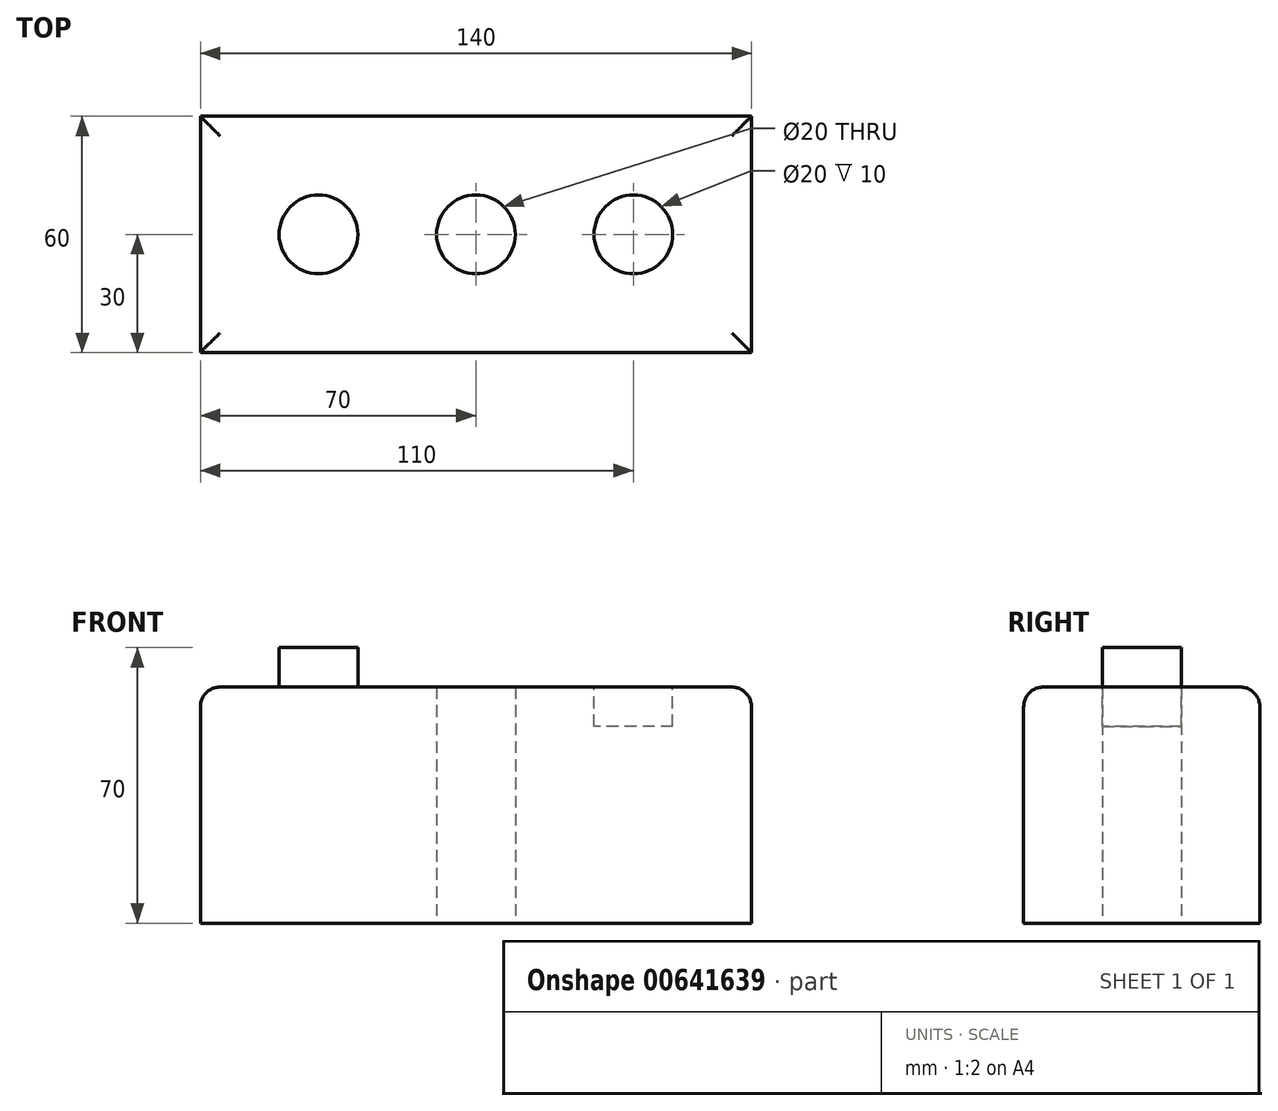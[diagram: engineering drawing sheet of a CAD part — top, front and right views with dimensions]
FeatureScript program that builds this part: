
annotation { "Feature Type Name" : "Feature", "Feature Type Description" : "" }
export const myFeature = defineFeature(function(context is Context, id is Id, definition is map)
    precondition{}
    {
        {
            var Q0;
            Q0=qCreatedBy(makeId("Top.planeOp"),FACE);
            var sketch = newSketch(context, id + "F0", { "sketchPlane" : qUnion([Q0])});
            skLineSegment(sketch, "E0.bottom", {"start": v(70, -30) * mm, "end": v(-70, -30) * mm});
            skLineSegment(sketch, "E0.top", {"start": v(70, 30) * mm, "end": v(-70, 30) * mm});
            skLineSegment(sketch, "E0.left", {"start": v(70, -30) * mm, "end": v(70, 30) * mm});
            skLineSegment(sketch, "E0.right", {"start": v(-70, -30) * mm, "end": v(-70, 30) * mm});
            skPoint(sketch, "E0.middle", {"position": v(0, 0) * mm});
            skSolve(sketch);
        }
        {
            var Q0;
            Q0=makeQuery(id+"F0.imprint","IMPRINT",FACE,{"disambiguationData":[TD([[makeQuery(id+"F0.imprint","IMPRINT",EDGE,{"derivedFrom":sQuery(id+"F0.wireOp",EDGE,"E0.bottom")}),-1.0]])]});
            var sketch = newSketch(context, id + "F1", { "sketchPlane" : qUnion([Q0])});
            skCircle(sketch, "E1", {"center": v(-40, 0) * mm, "radius": 10 * mm});
            skSolve(sketch);
        }
        {
            var Q0;
            Q0=makeQuery(id+"F0.imprint","IMPRINT",FACE,{"disambiguationData":[TD([[makeQuery(id+"F0.imprint","IMPRINT",EDGE,{"derivedFrom":sQuery(id+"F0.wireOp",EDGE,"E0.bottom")}),-1.0]])]});
            var sketch = newSketch(context, id + "F2", { "sketchPlane" : qUnion([Q0])});
            skCircle(sketch, "E2", {"center": v(0, 0) * mm, "radius": 10 * mm});
            skSolve(sketch);
        }
        {
            var Q0;
            Q0 = qSketchRegion(id + "F0", true);
            extrude(context, id + "F3", {"entities" : qUnion([Q0]), "depth" : 60 * mm, "offsetDistance" : 25 * mm});
        }
        {
            var Q0;
            Q0 = qSketchRegion(id + "F1", true);
            extrude(context, id + "F4", {"entities" : qUnion([Q0]), "operationType" : NewBodyOperationType.ADD, "depth" : 70 * mm, "offsetDistance" : 25 * mm});
        }
        {
            var Q0;
            Q0 = qSketchRegion(id + "F2", true);
            extrude(context, id + "F5", {"entities" : qUnion([Q0]), "operationType" : NewBodyOperationType.REMOVE, "depth" : 120.3 * mm, "offsetDistance" : 25 * mm});
        }
        {
            var Q0;
            Q0=makeQuery(id+"F3.opExtrude","CAP_FACE",FACE,{"disambiguationData":[OSD([sQuery(id+"F0.wireOp",EDGE,"E0.bottom"),sQuery(id+"F0.wireOp",EDGE,"E0.top"),sQuery(id+"F0.wireOp",EDGE,"E0.left"),sQuery(id+"F0.wireOp",EDGE,"E0.right")])],"isStart":false});
            var sketch = newSketch(context, id + "F6", { "sketchPlane" : qUnion([Q0])});
            skCircle(sketch, "E3", {"center": v(40, 0) * mm, "radius": 10 * mm});
            skSolve(sketch);
        }
        {
            var Q0;
            Q0 = qSketchRegion(id + "F6", true);
            extrude(context, id + "F7", {"entities" : qUnion([Q0]), "operationType" : NewBodyOperationType.REMOVE, "oppositeDirection" : true, "depth" : 10 * mm, "offsetDistance" : 25 * mm});
        }
        {
            var Q0;
            Q0=makeQuery(id+"F3.opExtrude","CAP_EDGE",EDGE,{"disambiguationData":[OSD([sQuery(id+"F0.wireOp",EDGE,"E0.top")])],"isStart":false});
            var Q1;
            Q1=makeQuery(id+"F3.opExtrude","CAP_EDGE",EDGE,{"disambiguationData":[OSD([sQuery(id+"F0.wireOp",EDGE,"E0.right")])],"isStart":false});
            var Q2;
            Q2=makeQuery(id+"F3.opExtrude","CAP_EDGE",EDGE,{"disambiguationData":[OSD([sQuery(id+"F0.wireOp",EDGE,"E0.bottom")])],"isStart":false});
            var Q3;
            Q3=makeQuery(id+"F3.opExtrude","CAP_EDGE",EDGE,{"disambiguationData":[OSD([sQuery(id+"F0.wireOp",EDGE,"E0.left")])],"isStart":false});
            fillet(context, id + "F8", {"entities" : qUnion([Q0, Q1, Q2, Q3]), "radius" : 5 * mm, "tangentPropagation" : true, "allowEdgeOverflow" : false});
        }
    });
